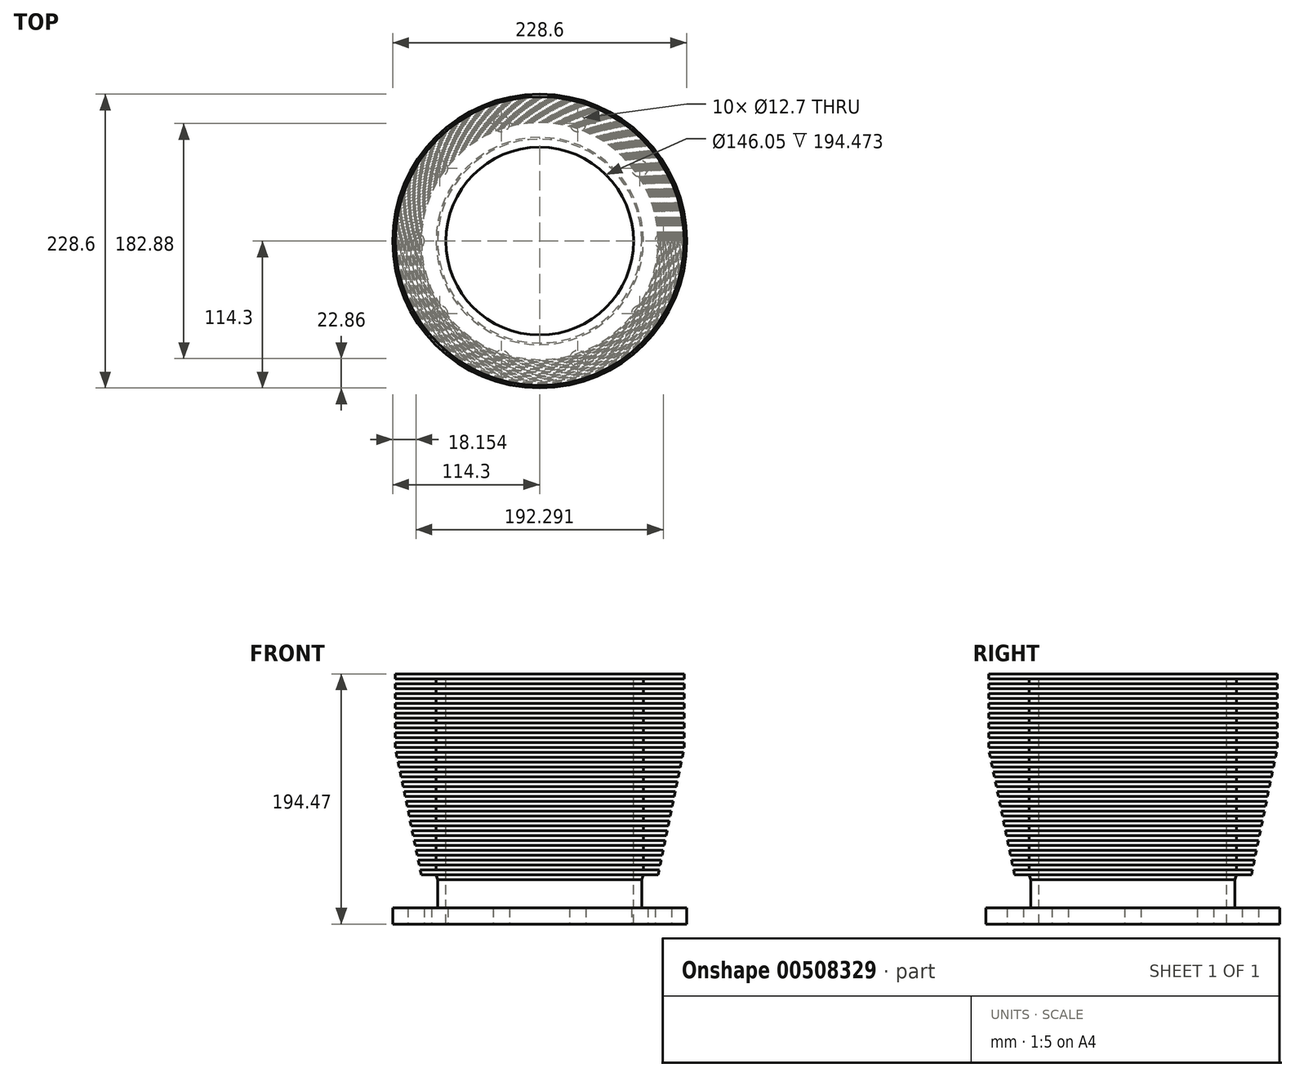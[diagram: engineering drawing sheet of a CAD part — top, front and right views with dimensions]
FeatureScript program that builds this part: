
annotation { "Feature Type Name" : "Feature", "Feature Type Description" : "" }
export const myFeature = defineFeature(function(context is Context, id is Id, definition is map)
    precondition{}
    {
        {
            var Q0;
            Q0=qCreatedBy(makeId("Front.planeOp"),FACE);
            var sketch = newSketch(context, id + "F0", { "sketchPlane" : qUnion([Q0])});
            skLineSegment(sketch, "E0", {"start": v(-73.03, 98.28) * mm, "end": v(-73.02, -96.2) * mm});
            skLineSegment(sketch, "E1", {"start": v(-73.03, 98.28) * mm, "end": v(-113.66, 98.28) * mm});
            skLineSegment(sketch, "E2", {"start": v(-113.66, 98.28) * mm, "end": v(-113.66, 94.47) * mm});
            skLineSegment(sketch, "E3", {"start": v(-73.03, -96.2) * mm, "end": v(-114.3, -96.2) * mm});
            skLineSegment(sketch, "E4", {"start": v(-114.3, -96.2) * mm, "end": v(-114.3, -83.5) * mm});
            skLineSegment(sketch, "E5", {"start": v(-114.3, -83.5) * mm, "end": v(-89.24, -83.5) * mm});
            skLineSegment(sketch, "E6", {"start": v(-91.44, -112.83) * mm, "end": v(-91.44, -64.67) * mm, "construction": true});
            skLineSegment(sketch, "E7", {"start": v(-91.44, -70.36) * mm, "end": v(-97.8, -70.36) * mm, "construction": true});
            skLineSegment(sketch, "E8.MirrorCS", {"start": v(-91.44, -70.36) * mm, "end": v(-85.1, -70.36) * mm, "construction": true});
            skLineSegment(sketch, "E9", {"start": v(-89.24, -83.5) * mm, "end": v(-79.37, -83.5) * mm});
            skLineSegment(sketch, "E10", {"start": v(-113.66, 94.47) * mm, "end": v(-80.65, 94.47) * mm});
            skLineSegment(sketch, "E11", {"start": v(-80.65, 90.66) * mm, "end": v(-113.66, 90.66) * mm});
            skLineSegment(sketch, "E12", {"start": v(-113.66, 90.66) * mm, "end": v(-113.66, 86.85) * mm});
            skLineSegment(sketch, "E13", {"start": v(-113.66, 86.85) * mm, "end": v(-80.65, 86.85) * mm});
            skLineSegment(sketch, "E14", {"start": v(-80.65, 86.85) * mm, "end": v(-80.65, 83.04) * mm});
            skLineSegment(sketch, "E15", {"start": v(-80.65, 83.04) * mm, "end": v(-113.66, 83.04) * mm});
            skLineSegment(sketch, "E16", {"start": v(-113.66, 83.04) * mm, "end": v(-113.66, 79.23) * mm});
            skLineSegment(sketch, "E17", {"start": v(-113.66, 79.23) * mm, "end": v(-80.65, 79.23) * mm});
            skLineSegment(sketch, "E18", {"start": v(-80.65, 79.23) * mm, "end": v(-80.65, 75.42) * mm});
            skLineSegment(sketch, "E19", {"start": v(-80.65, 75.42) * mm, "end": v(-113.67, 75.42) * mm});
            skLineSegment(sketch, "E20", {"start": v(-113.67, 75.42) * mm, "end": v(-113.67, 71.61) * mm});
            skLineSegment(sketch, "E21", {"start": v(-113.67, 71.61) * mm, "end": v(-80.65, 71.61) * mm});
            skLineSegment(sketch, "E22", {"start": v(-80.65, 71.61) * mm, "end": v(-80.65, 67.8) * mm});
            skLineSegment(sketch, "E23", {"start": v(-80.65, 67.8) * mm, "end": v(-113.67, 67.8) * mm});
            skLineSegment(sketch, "E24", {"start": v(-113.67, 67.8) * mm, "end": v(-113.67, 64) * mm});
            skLineSegment(sketch, "E25", {"start": v(-113.67, 64) * mm, "end": v(-80.65, 64) * mm});
            skLineSegment(sketch, "E26", {"start": v(-80.65, 64) * mm, "end": v(-80.64, 60.18) * mm});
            skLineSegment(sketch, "E27", {"start": v(-80.65, 60.18) * mm, "end": v(-113.67, 60.18) * mm});
            skLineSegment(sketch, "E28", {"start": v(-113.67, 60.18) * mm, "end": v(-113.67, 56.37) * mm});
            skLineSegment(sketch, "E29", {"start": v(-113.67, 56.37) * mm, "end": v(-80.65, 56.37) * mm});
            skLineSegment(sketch, "E30.0.1.0", {"start": v(-113.67, 48.75) * mm, "end": v(-80.65, 48.75) * mm});
            skLineSegment(sketch, "E30.0.1.1", {"start": v(-113.67, 52.56) * mm, "end": v(-113.67, 48.75) * mm});
            skLineSegment(sketch, "E30.0.1.2", {"start": v(-80.65, 52.56) * mm, "end": v(-113.67, 52.56) * mm});
            skLineSegment(sketch, "E30.0.2.0", {"start": v(-113.67, 41.13) * mm, "end": v(-80.65, 41.13) * mm});
            skLineSegment(sketch, "E30.0.2.1", {"start": v(-113.67, 44.94) * mm, "end": v(-113.67, 41.13) * mm});
            skLineSegment(sketch, "E30.0.2.2", {"start": v(-80.65, 44.94) * mm, "end": v(-113.67, 44.94) * mm});
            skLineSegment(sketch, "E30.0.3.0", {"start": v(-113.67, 33.51) * mm, "end": v(-80.65, 33.51) * mm});
            skLineSegment(sketch, "E30.0.3.1", {"start": v(-113.67, 37.32) * mm, "end": v(-113.67, 33.51) * mm});
            skLineSegment(sketch, "E30.0.3.2", {"start": v(-80.65, 37.32) * mm, "end": v(-113.67, 37.32) * mm});
            skLineSegment(sketch, "E30.0.4.0", {"start": v(-113.67, 25.9) * mm, "end": v(-80.65, 25.9) * mm});
            skLineSegment(sketch, "E30.0.4.1", {"start": v(-113.67, 29.7) * mm, "end": v(-113.67, 25.9) * mm});
            skLineSegment(sketch, "E30.0.4.2", {"start": v(-80.65, 29.7) * mm, "end": v(-113.67, 29.7) * mm});
            skLineSegment(sketch, "E30.direction1", {"start": v(-113.67, 56.37) * mm, "end": v(-87, 56.37) * mm, "construction": true});
            skLineSegment(sketch, "E30.direction2", {"start": v(-113.67, 56.37) * mm, "end": v(-113.67, 48.75) * mm, "construction": true});
            skLineSegment(sketch, "E31.0.0.5", {"start": v(-113.67, 18.27) * mm, "end": v(-80.65, 18.27) * mm});
            skLineSegment(sketch, "E31.3.0.5", {"start": v(-113.67, 22.08) * mm, "end": v(-113.67, 18.27) * mm});
            skLineSegment(sketch, "E31.6.0.5", {"start": v(-80.65, 22.08) * mm, "end": v(-113.67, 22.08) * mm});
            skLineSegment(sketch, "E31.0.0.6", {"start": v(-113.67, 10.65) * mm, "end": v(-80.65, 10.65) * mm});
            skLineSegment(sketch, "E31.3.0.6", {"start": v(-113.67, 14.46) * mm, "end": v(-113.67, 10.65) * mm});
            skLineSegment(sketch, "E31.6.0.6", {"start": v(-80.65, 14.46) * mm, "end": v(-113.67, 14.46) * mm});
            skLineSegment(sketch, "E31.0.0.7", {"start": v(-113.67, 3.03) * mm, "end": v(-80.65, 3.03) * mm});
            skLineSegment(sketch, "E31.3.0.7", {"start": v(-113.67, 6.84) * mm, "end": v(-113.67, 3.03) * mm});
            skLineSegment(sketch, "E31.6.0.7", {"start": v(-80.65, 6.84) * mm, "end": v(-113.67, 6.84) * mm});
            skLineSegment(sketch, "E31.0.0.8", {"start": v(-113.67, -4.59) * mm, "end": v(-80.65, -4.59) * mm});
            skLineSegment(sketch, "E31.3.0.8", {"start": v(-113.67, -0.78) * mm, "end": v(-113.67, -4.59) * mm});
            skLineSegment(sketch, "E31.6.0.8", {"start": v(-80.65, -0.78) * mm, "end": v(-113.67, -0.78) * mm});
            skLineSegment(sketch, "E31.0.0.9", {"start": v(-113.67, -12.2) * mm, "end": v(-80.65, -12.2) * mm});
            skLineSegment(sketch, "E31.3.0.9", {"start": v(-113.67, -8.4) * mm, "end": v(-113.67, -12.2) * mm});
            skLineSegment(sketch, "E31.6.0.9", {"start": v(-80.65, -8.4) * mm, "end": v(-113.67, -8.4) * mm});
            skLineSegment(sketch, "E31.0.0.10", {"start": v(-113.67, -19.83) * mm, "end": v(-80.65, -19.83) * mm});
            skLineSegment(sketch, "E31.3.0.10", {"start": v(-113.67, -16.02) * mm, "end": v(-113.67, -19.83) * mm});
            skLineSegment(sketch, "E31.6.0.10", {"start": v(-80.65, -16.02) * mm, "end": v(-113.67, -16.02) * mm});
            skLineSegment(sketch, "E31.0.0.11", {"start": v(-113.67, -27.45) * mm, "end": v(-80.65, -27.45) * mm});
            skLineSegment(sketch, "E31.3.0.11", {"start": v(-113.67, -23.64) * mm, "end": v(-113.67, -27.45) * mm});
            skLineSegment(sketch, "E31.6.0.11", {"start": v(-80.65, -23.64) * mm, "end": v(-113.67, -23.64) * mm});
            skLineSegment(sketch, "E31.0.0.12", {"start": v(-113.67, -35.07) * mm, "end": v(-80.65, -35.07) * mm});
            skLineSegment(sketch, "E31.3.0.12", {"start": v(-113.67, -31.26) * mm, "end": v(-113.67, -35.07) * mm});
            skLineSegment(sketch, "E31.6.0.12", {"start": v(-80.65, -31.26) * mm, "end": v(-113.67, -31.26) * mm});
            skLineSegment(sketch, "E31.0.0.13", {"start": v(-113.67, -42.69) * mm, "end": v(-80.65, -42.69) * mm});
            skLineSegment(sketch, "E31.3.0.13", {"start": v(-113.67, -38.88) * mm, "end": v(-113.67, -42.69) * mm});
            skLineSegment(sketch, "E31.6.0.13", {"start": v(-80.65, -38.88) * mm, "end": v(-113.67, -38.88) * mm});
            skLineSegment(sketch, "E31.0.0.14", {"start": v(-113.67, -50.3) * mm, "end": v(-80.65, -50.3) * mm});
            skLineSegment(sketch, "E31.3.0.14", {"start": v(-113.67, -46.5) * mm, "end": v(-113.67, -50.3) * mm});
            skLineSegment(sketch, "E31.6.0.14", {"start": v(-80.65, -46.5) * mm, "end": v(-113.67, -46.5) * mm});
            skLineSegment(sketch, "E31.0.0.15", {"start": v(-113.67, -57.93) * mm, "end": v(-80.65, -57.93) * mm});
            skLineSegment(sketch, "E31.3.0.15", {"start": v(-113.67, -54.12) * mm, "end": v(-113.67, -57.93) * mm});
            skLineSegment(sketch, "E31.6.0.15", {"start": v(-80.65, -54.12) * mm, "end": v(-113.67, -54.12) * mm});
            skLineSegment(sketch, "E32", {"start": v(-80.65, 94.47) * mm, "end": v(-80.65, 90.66) * mm});
            skLineSegment(sketch, "E33", {"start": v(-80.65, 56.37) * mm, "end": v(-80.65, 52.56) * mm});
            skLineSegment(sketch, "E34", {"start": v(-80.65, 48.75) * mm, "end": v(-80.65, 44.94) * mm});
            skLineSegment(sketch, "E35", {"start": v(-80.65, 41.13) * mm, "end": v(-80.65, 37.32) * mm});
            skLineSegment(sketch, "E36", {"start": v(-80.65, 33.51) * mm, "end": v(-80.65, 29.7) * mm});
            skLineSegment(sketch, "E37", {"start": v(-80.65, 25.9) * mm, "end": v(-80.65, 22.08) * mm});
            skLineSegment(sketch, "E38", {"start": v(-80.65, 18.27) * mm, "end": v(-80.65, 14.46) * mm});
            skLineSegment(sketch, "E39", {"start": v(-80.65, 10.65) * mm, "end": v(-80.65, 6.84) * mm});
            skLineSegment(sketch, "E40", {"start": v(-80.65, 3.03) * mm, "end": v(-80.65, -0.78) * mm});
            skLineSegment(sketch, "E41", {"start": v(-80.65, -4.59) * mm, "end": v(-80.65, -8.4) * mm});
            skLineSegment(sketch, "E42", {"start": v(-80.65, -12.2) * mm, "end": v(-80.65, -16.02) * mm});
            skLineSegment(sketch, "E43", {"start": v(-80.65, -19.83) * mm, "end": v(-80.65, -23.64) * mm});
            skLineSegment(sketch, "E44", {"start": v(-80.65, -27.45) * mm, "end": v(-80.65, -31.26) * mm});
            skLineSegment(sketch, "E45", {"start": v(-80.65, -35.07) * mm, "end": v(-80.65, -38.88) * mm});
            skLineSegment(sketch, "E46", {"start": v(-80.65, -42.69) * mm, "end": v(-80.65, -46.5) * mm});
            skLineSegment(sketch, "E47", {"start": v(-80.64, -53.01) * mm, "end": v(-80.64, -50.3) * mm});
            skLineSegment(sketch, "E48", {"start": v(-80.64, -54.12) * mm, "end": v(-80.65, -53.01) * mm});
            skLineSegment(sketch, "E49", {"start": v(-80.65, -57.93) * mm, "end": v(-79.38, -61.74) * mm});
            skLineSegment(sketch, "E50", {"start": v(-79.37, -65.55) * mm, "end": v(-79.37, -83.5) * mm});
            skLineSegment(sketch, "E51", {"start": v(0, 62.29) * mm, "end": v(0, -119.91) * mm, "construction": true});
            skLineSegment(sketch, "E52", {"start": v(-79.38, -65.55) * mm, "end": v(-79.37, -61.74) * mm});
            skSolve(sketch);
        }
        {
            var Q0;
            Q0=makeQuery(id+"F0.imprint","IMPRINT",FACE,{"disambiguationData":[TD([[makeQuery(id+"F0.imprint","IMPRINT",EDGE,{"derivedFrom":sQuery(id+"F0.wireOp",EDGE,"E0")}),-1.0]])]});
            var Q1;
            Q1=sQuery(id+"F0.wireOp",EDGE,"E51");
            revolve(context, id + "F1", {"entities" : qUnion([Q0]), "axis" : qUnion([Q1]), "revolveType" : RevolveType.FULL});
        }
        {
            var Q0;
            Q0=qCreatedBy(makeId("Front.planeOp"),FACE);
            var sketch = newSketch(context, id + "F2", { "sketchPlane" : qUnion([Q0])});
            skLineSegment(sketch, "E53", {"start": v(-90.02, -68.33) * mm, "end": v(-112.33, 40.34) * mm});
            skLineSegment(sketch, "E54", {"start": v(-167.23, 55.17) * mm, "end": v(-167.23, -75.34) * mm});
            skLineSegment(sketch, "E55", {"start": v(-167.23, -75.34) * mm, "end": v(-90.25, -75.34) * mm});
            skLineSegment(sketch, "E56", {"start": v(-90.25, -75.34) * mm, "end": v(-90.02, -68.33) * mm});
            skLineSegment(sketch, "E57", {"start": v(0, 0) * mm, "end": v(0, 114.86) * mm, "construction": true});
            skLineSegment(sketch, "E58", {"start": v(-112.33, 40.34) * mm, "end": v(-112.33, 54.9) * mm});
            skLineSegment(sketch, "E59", {"start": v(-112.33, 54.9) * mm, "end": v(-112.33, 99.65) * mm});
            skLineSegment(sketch, "E60", {"start": v(-112.33, 99.65) * mm, "end": v(-98.72, 123) * mm});
            skLineSegment(sketch, "E61", {"start": v(-98.72, 123) * mm, "end": v(-167.23, 55.17) * mm});
            skSolve(sketch);
        }
        {
            var Q0;
            Q0=makeQuery(id+"F2.imprint","IMPRINT",FACE,{"disambiguationData":[TD([[makeQuery(id+"F2.imprint","IMPRINT",EDGE,{"derivedFrom":sQuery(id+"F2.wireOp",EDGE,"E53")}),1.0]])]});
            var Q1;
            Q1=sQuery(id+"F2.wireOp",EDGE,"E57");
            revolve(context, id + "F3", {"operationType" : NewBodyOperationType.REMOVE, "entities" : qUnion([Q0]), "axis" : qUnion([Q1]), "revolveType" : RevolveType.FULL, "oppositeDirection" : true});
        }
        {
            var Q0;
            Q0=makeQuery(id+"F1.opRevolve","SWEPT_FACE",FACE,{"disambiguationData":[OSD([sQuery(id+"F0.wireOp",EDGE,"E3")])]});
            var sketch = newSketch(context, id + "F4", { "sketchPlane" : qUnion([Q0])});
            skCircle(sketch, "E62.cCircle", {"center": v(0, 0) * mm, "radius": 91.44 * mm, "construction": true});
            skLineSegment(sketch, "E62.0", {"start": v(-29.71, 91.44) * mm, "end": v(29.71, 91.44) * mm});
            skLineSegment(sketch, "E62.1", {"start": v(29.71, 91.44) * mm, "end": v(77.78, 56.51) * mm});
            skLineSegment(sketch, "E62.2", {"start": v(77.78, 56.51) * mm, "end": v(96.15, 0) * mm});
            skLineSegment(sketch, "E62.3", {"start": v(96.15, 0) * mm, "end": v(77.78, -56.51) * mm});
            skLineSegment(sketch, "E62.4", {"start": v(77.78, -56.51) * mm, "end": v(29.71, -91.44) * mm});
            skLineSegment(sketch, "E62.5", {"start": v(29.71, -91.44) * mm, "end": v(-29.71, -91.44) * mm});
            skLineSegment(sketch, "E62.6", {"start": v(-29.71, -91.44) * mm, "end": v(-77.78, -56.51) * mm});
            skLineSegment(sketch, "E62.7", {"start": v(-77.78, -56.51) * mm, "end": v(-96.15, 0) * mm});
            skLineSegment(sketch, "E62.8", {"start": v(-96.15, 0) * mm, "end": v(-77.78, 56.51) * mm});
            skLineSegment(sketch, "E62.9", {"start": v(-77.78, 56.51) * mm, "end": v(-29.71, 91.44) * mm});
            skPoint(sketch, "E62.0.midPoint", {"position": v(0, 91.44) * mm});
            skCircle(sketch, "E63", {"center": v(-29.71, 91.44) * mm, "radius": 6.35 * mm});
            skCircle(sketch, "E64.1.0", {"center": v(-77.78, 56.51) * mm, "radius": 6.35 * mm});
            skCircle(sketch, "E64.2.0", {"center": v(-96.15, 0) * mm, "radius": 6.35 * mm});
            skCircle(sketch, "E64.3.0", {"center": v(-77.78, -56.51) * mm, "radius": 6.35 * mm});
            skCircle(sketch, "E64.4.0", {"center": v(-29.71, -91.44) * mm, "radius": 6.35 * mm});
            skCircle(sketch, "E64.5.0", {"center": v(29.71, -91.44) * mm, "radius": 6.35 * mm});
            skCircle(sketch, "E64.6.0", {"center": v(77.78, -56.51) * mm, "radius": 6.35 * mm});
            skCircle(sketch, "E64.7.0", {"center": v(96.15, 0) * mm, "radius": 6.35 * mm});
            skCircle(sketch, "E64.8.0", {"center": v(77.78, 56.51) * mm, "radius": 6.35 * mm});
            skCircle(sketch, "E64.9.0", {"center": v(29.71, 91.44) * mm, "radius": 6.35 * mm});
            skSolve(sketch);
        }
        {
            var Q0;
            {var subQ0=sQuery(id+"F4.wireOp",EDGE,"E62.9");var subQ1=sQuery(id+"F4.wireOp",EDGE,"E62.0");var subQ2=makeQuery(id+"F4.imprint","INTERSECT",VERTEX,{"derivedFrom":[subQ1,subQ0]});Q0=makeQuery(id+"F4.imprint","IMPRINT",FACE,{"disambiguationData":[TD([[makeQuery(id+"F4.imprint","IMPRINT",EDGE,{"disambiguationData":[TD([[subQ2,-1.0]])],"derivedFrom":subQ1}),1.0]])]});}
            var Q1;
            {var subQ0=sQuery(id+"F4.wireOp",EDGE,"E62.9");var subQ1=sQuery(id+"F4.wireOp",EDGE,"E62.0");var subQ2=makeQuery(id+"F4.imprint","INTERSECT",VERTEX,{"derivedFrom":[subQ1,subQ0]});Q1=makeQuery(id+"F4.imprint","IMPRINT",FACE,{"disambiguationData":[TD([[makeQuery(id+"F4.imprint","IMPRINT",EDGE,{"disambiguationData":[TD([[subQ2,-1.0]])],"derivedFrom":subQ1}),-1.0]])]});}
            var Q2;
            {var subQ0=sQuery(id+"F4.wireOp",EDGE,"E62.1");var subQ1=sQuery(id+"F4.wireOp",EDGE,"E62.0");var subQ2=makeQuery(id+"F4.imprint","INTERSECT",VERTEX,{"derivedFrom":[subQ1,subQ0]});Q2=makeQuery(id+"F4.imprint","IMPRINT",FACE,{"disambiguationData":[TD([[makeQuery(id+"F4.imprint","IMPRINT",EDGE,{"disambiguationData":[TD([[subQ2,1.0]])],"derivedFrom":subQ1}),1.0]])]});}
            var Q3;
            {var subQ0=sQuery(id+"F4.wireOp",EDGE,"E62.1");var subQ1=sQuery(id+"F4.wireOp",EDGE,"E62.0");var subQ2=makeQuery(id+"F4.imprint","INTERSECT",VERTEX,{"derivedFrom":[subQ1,subQ0]});Q3=makeQuery(id+"F4.imprint","IMPRINT",FACE,{"disambiguationData":[TD([[makeQuery(id+"F4.imprint","IMPRINT",EDGE,{"disambiguationData":[TD([[subQ2,1.0]])],"derivedFrom":subQ1}),-1.0]])]});}
            var Q4;
            {var subQ0=sQuery(id+"F4.wireOp",EDGE,"E62.2");var subQ1=sQuery(id+"F4.wireOp",EDGE,"E62.1");var subQ2=makeQuery(id+"F4.imprint","INTERSECT",VERTEX,{"derivedFrom":[subQ1,subQ0]});Q4=makeQuery(id+"F4.imprint","IMPRINT",FACE,{"disambiguationData":[TD([[makeQuery(id+"F4.imprint","IMPRINT",EDGE,{"disambiguationData":[TD([[subQ2,1.0]])],"derivedFrom":subQ1}),1.0]])]});}
            var Q5;
            {var subQ0=sQuery(id+"F4.wireOp",EDGE,"E62.2");var subQ1=sQuery(id+"F4.wireOp",EDGE,"E62.1");var subQ2=makeQuery(id+"F4.imprint","INTERSECT",VERTEX,{"derivedFrom":[subQ1,subQ0]});Q5=makeQuery(id+"F4.imprint","IMPRINT",FACE,{"disambiguationData":[TD([[makeQuery(id+"F4.imprint","IMPRINT",EDGE,{"disambiguationData":[TD([[subQ2,1.0]])],"derivedFrom":subQ1}),-1.0]])]});}
            var Q6;
            {var subQ0=sQuery(id+"F4.wireOp",EDGE,"E62.3");var subQ1=sQuery(id+"F4.wireOp",EDGE,"E62.2");var subQ2=makeQuery(id+"F4.imprint","INTERSECT",VERTEX,{"derivedFrom":[subQ1,subQ0]});Q6=makeQuery(id+"F4.imprint","IMPRINT",FACE,{"disambiguationData":[TD([[makeQuery(id+"F4.imprint","IMPRINT",EDGE,{"disambiguationData":[TD([[subQ2,1.0]])],"derivedFrom":subQ1}),1.0]])]});}
            var Q7;
            {var subQ0=sQuery(id+"F4.wireOp",EDGE,"E62.3");var subQ1=sQuery(id+"F4.wireOp",EDGE,"E62.2");var subQ2=makeQuery(id+"F4.imprint","INTERSECT",VERTEX,{"derivedFrom":[subQ1,subQ0]});Q7=makeQuery(id+"F4.imprint","IMPRINT",FACE,{"disambiguationData":[TD([[makeQuery(id+"F4.imprint","IMPRINT",EDGE,{"disambiguationData":[TD([[subQ2,1.0]])],"derivedFrom":subQ1}),-1.0]])]});}
            var Q8;
            {var subQ0=sQuery(id+"F4.wireOp",EDGE,"E62.4");var subQ1=sQuery(id+"F4.wireOp",EDGE,"E62.3");var subQ2=makeQuery(id+"F4.imprint","INTERSECT",VERTEX,{"derivedFrom":[subQ1,subQ0]});Q8=makeQuery(id+"F4.imprint","IMPRINT",FACE,{"disambiguationData":[TD([[makeQuery(id+"F4.imprint","IMPRINT",EDGE,{"disambiguationData":[TD([[subQ2,1.0]])],"derivedFrom":subQ1}),1.0]])]});}
            var Q9;
            {var subQ0=sQuery(id+"F4.wireOp",EDGE,"E62.4");var subQ1=sQuery(id+"F4.wireOp",EDGE,"E62.3");var subQ2=makeQuery(id+"F4.imprint","INTERSECT",VERTEX,{"derivedFrom":[subQ1,subQ0]});Q9=makeQuery(id+"F4.imprint","IMPRINT",FACE,{"disambiguationData":[TD([[makeQuery(id+"F4.imprint","IMPRINT",EDGE,{"disambiguationData":[TD([[subQ2,1.0]])],"derivedFrom":subQ1}),-1.0]])]});}
            var Q10;
            {var subQ0=sQuery(id+"F4.wireOp",EDGE,"E62.5");var subQ1=sQuery(id+"F4.wireOp",EDGE,"E62.4");var subQ2=makeQuery(id+"F4.imprint","INTERSECT",VERTEX,{"derivedFrom":[subQ1,subQ0]});Q10=makeQuery(id+"F4.imprint","IMPRINT",FACE,{"disambiguationData":[TD([[makeQuery(id+"F4.imprint","IMPRINT",EDGE,{"disambiguationData":[TD([[subQ2,1.0]])],"derivedFrom":subQ1}),-1.0]])]});}
            var Q11;
            {var subQ0=sQuery(id+"F4.wireOp",EDGE,"E62.5");var subQ1=sQuery(id+"F4.wireOp",EDGE,"E62.4");var subQ2=makeQuery(id+"F4.imprint","INTERSECT",VERTEX,{"derivedFrom":[subQ1,subQ0]});Q11=makeQuery(id+"F4.imprint","IMPRINT",FACE,{"disambiguationData":[TD([[makeQuery(id+"F4.imprint","IMPRINT",EDGE,{"disambiguationData":[TD([[subQ2,1.0]])],"derivedFrom":subQ1}),1.0]])]});}
            var Q12;
            {var subQ0=sQuery(id+"F4.wireOp",EDGE,"E62.6");var subQ1=sQuery(id+"F4.wireOp",EDGE,"E62.5");var subQ2=makeQuery(id+"F4.imprint","INTERSECT",VERTEX,{"derivedFrom":[subQ1,subQ0]});Q12=makeQuery(id+"F4.imprint","IMPRINT",FACE,{"disambiguationData":[TD([[makeQuery(id+"F4.imprint","IMPRINT",EDGE,{"disambiguationData":[TD([[subQ2,1.0]])],"derivedFrom":subQ1}),1.0]])]});}
            var Q13;
            {var subQ0=sQuery(id+"F4.wireOp",EDGE,"E62.6");var subQ1=sQuery(id+"F4.wireOp",EDGE,"E62.5");var subQ2=makeQuery(id+"F4.imprint","INTERSECT",VERTEX,{"derivedFrom":[subQ1,subQ0]});Q13=makeQuery(id+"F4.imprint","IMPRINT",FACE,{"disambiguationData":[TD([[makeQuery(id+"F4.imprint","IMPRINT",EDGE,{"disambiguationData":[TD([[subQ2,1.0]])],"derivedFrom":subQ1}),-1.0]])]});}
            var Q14;
            {var subQ0=sQuery(id+"F4.wireOp",EDGE,"E62.7");var subQ1=sQuery(id+"F4.wireOp",EDGE,"E62.6");var subQ2=makeQuery(id+"F4.imprint","INTERSECT",VERTEX,{"derivedFrom":[subQ1,subQ0]});Q14=makeQuery(id+"F4.imprint","IMPRINT",FACE,{"disambiguationData":[TD([[makeQuery(id+"F4.imprint","IMPRINT",EDGE,{"disambiguationData":[TD([[subQ2,1.0]])],"derivedFrom":subQ1}),1.0]])]});}
            var Q15;
            {var subQ0=sQuery(id+"F4.wireOp",EDGE,"E62.7");var subQ1=sQuery(id+"F4.wireOp",EDGE,"E62.6");var subQ2=makeQuery(id+"F4.imprint","INTERSECT",VERTEX,{"derivedFrom":[subQ1,subQ0]});Q15=makeQuery(id+"F4.imprint","IMPRINT",FACE,{"disambiguationData":[TD([[makeQuery(id+"F4.imprint","IMPRINT",EDGE,{"disambiguationData":[TD([[subQ2,1.0]])],"derivedFrom":subQ1}),-1.0]])]});}
            var Q16;
            {var subQ0=sQuery(id+"F4.wireOp",EDGE,"E62.8");var subQ1=sQuery(id+"F4.wireOp",EDGE,"E62.7");var subQ2=makeQuery(id+"F4.imprint","INTERSECT",VERTEX,{"derivedFrom":[subQ1,subQ0]});Q16=makeQuery(id+"F4.imprint","IMPRINT",FACE,{"disambiguationData":[TD([[makeQuery(id+"F4.imprint","IMPRINT",EDGE,{"disambiguationData":[TD([[subQ2,1.0]])],"derivedFrom":subQ1}),1.0]])]});}
            var Q17;
            {var subQ0=sQuery(id+"F4.wireOp",EDGE,"E62.8");var subQ1=sQuery(id+"F4.wireOp",EDGE,"E62.7");var subQ2=makeQuery(id+"F4.imprint","INTERSECT",VERTEX,{"derivedFrom":[subQ1,subQ0]});Q17=makeQuery(id+"F4.imprint","IMPRINT",FACE,{"disambiguationData":[TD([[makeQuery(id+"F4.imprint","IMPRINT",EDGE,{"disambiguationData":[TD([[subQ2,1.0]])],"derivedFrom":subQ1}),-1.0]])]});}
            var Q18;
            {var subQ0=sQuery(id+"F4.wireOp",EDGE,"E62.9");var subQ1=sQuery(id+"F4.wireOp",EDGE,"E62.8");var subQ2=makeQuery(id+"F4.imprint","INTERSECT",VERTEX,{"derivedFrom":[subQ1,subQ0]});Q18=makeQuery(id+"F4.imprint","IMPRINT",FACE,{"disambiguationData":[TD([[makeQuery(id+"F4.imprint","IMPRINT",EDGE,{"disambiguationData":[TD([[subQ2,1.0]])],"derivedFrom":subQ1}),1.0]])]});}
            var Q19;
            {var subQ0=sQuery(id+"F4.wireOp",EDGE,"E62.9");var subQ1=sQuery(id+"F4.wireOp",EDGE,"E62.8");var subQ2=makeQuery(id+"F4.imprint","INTERSECT",VERTEX,{"derivedFrom":[subQ1,subQ0]});Q19=makeQuery(id+"F4.imprint","IMPRINT",FACE,{"disambiguationData":[TD([[makeQuery(id+"F4.imprint","IMPRINT",EDGE,{"disambiguationData":[TD([[subQ2,1.0]])],"derivedFrom":subQ1}),-1.0]])]});}
            extrude(context, id + "F5", {"entities" : qUnion([Q0, Q1, Q2, Q3, Q4, Q5, Q6, Q7, Q8, Q9, Q10, Q11, Q12, Q13, Q14, Q15, Q16, Q17, Q18, Q19]), "operationType" : NewBodyOperationType.REMOVE, "oppositeDirection" : true, "depth" : 25.4 * mm, "offsetDistance" : 25.4 * mm});
        }
    });
